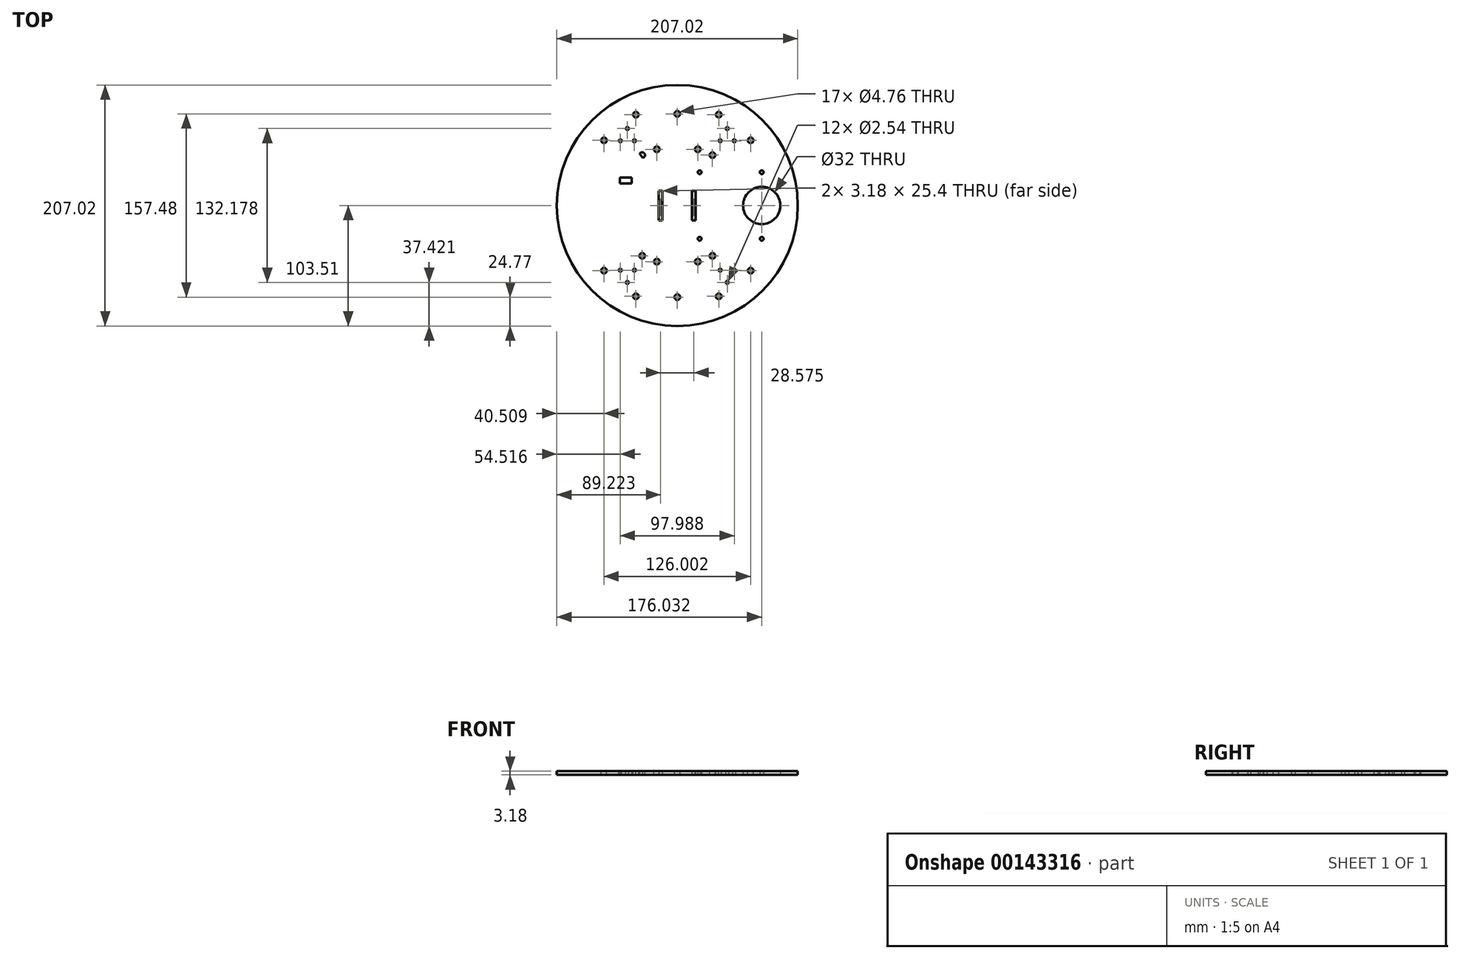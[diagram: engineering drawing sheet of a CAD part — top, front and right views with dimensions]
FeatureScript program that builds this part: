
annotation { "Feature Type Name" : "Feature", "Feature Type Description" : "" }
export const myFeature = defineFeature(function(context is Context, id is Id, definition is map)
    precondition{}
    {
        {
            var Q0;
            Q0=qCreatedBy(makeId("Top.planeOp"),FACE);
            var sketch = newSketch(context, id + "F0", { "sketchPlane" : qUnion([Q0])});
            skCircle(sketch, "E0", {"center": v(0, 0) * mm, "radius": 103.5 * mm});
            skLineSegment(sketch, "E1", {"start": v(-11.25, 102.9) * mm, "end": v(-11.25, 89.9) * mm});
            skLineSegment(sketch, "E2", {"start": v(-11.25, 89.9) * mm, "end": v(11.25, 89.9) * mm});
            skLineSegment(sketch, "E3", {"start": v(11.25, 89.9) * mm, "end": v(11.25, 102.9) * mm});
            skLineSegment(sketch, "E4", {"start": v(0, 89.9) * mm, "end": v(0, 0) * mm});
            skLineSegment(sketch, "E5.1.0", {"start": v(-83.48, -61.19) * mm, "end": v(-72.22, -54.69) * mm});
            skLineSegment(sketch, "E5.1.1", {"start": v(-72.22, -54.69) * mm, "end": v(-83.47, -35.2) * mm});
            skLineSegment(sketch, "E5.1.2", {"start": v(-83.47, -35.2) * mm, "end": v(-94.73, -41.7) * mm});
            skLineSegment(sketch, "E5.2.0", {"start": v(94.73, -41.7) * mm, "end": v(83.47, -35.2) * mm});
            skLineSegment(sketch, "E5.2.1", {"start": v(83.47, -35.2) * mm, "end": v(72.22, -54.69) * mm});
            skLineSegment(sketch, "E5.2.2", {"start": v(72.22, -54.69) * mm, "end": v(83.48, -61.19) * mm});
            skLineSegment(sketch, "E6", {"start": v(0, 0) * mm, "end": v(77.85, -44.95) * mm});
            skLineSegment(sketch, "E7", {"start": v(77.85, -44.95) * mm, "end": v(0, 0) * mm});
            skLineSegment(sketch, "E8", {"start": v(0, 0) * mm, "end": v(-77.85, -44.95) * mm});
            skSolve(sketch);
        }
        {
            var Q0;
            {var subQ2=sQuery(id+"F0.wireOp",EDGE,"E1");Q0=makeQuery(id+"F0.imprint","IMPRINT",FACE,{"disambiguationData":[TD([[makeQuery(id+"F0.imprint","IMPRINT",EDGE,{"derivedFrom":subQ2}),-1.0]])]});}
            var Q1;
            {var subQ0=sQuery(id+"F0.wireOp",EDGE,"E3");Q1=makeQuery(id+"F0.imprint","IMPRINT",FACE,{"disambiguationData":[TD([[makeQuery(id+"F0.imprint","IMPRINT",EDGE,{"derivedFrom":subQ0}),-1.0]])]});}
            var Q2;
            {var subQ4=sQuery(id+"F0.wireOp",EDGE,"E5.1.0");Q2=makeQuery(id+"F0.imprint","IMPRINT",FACE,{"disambiguationData":[TD([[makeQuery(id+"F0.imprint","IMPRINT",EDGE,{"derivedFrom":subQ4}),-1.0]])]});}
            var Q3;
            {var subQ3=sQuery(id+"F0.wireOp",EDGE,"E5.1.0");Q3=makeQuery(id+"F0.imprint","IMPRINT",FACE,{"disambiguationData":[TD([[makeQuery(id+"F0.imprint","IMPRINT",EDGE,{"derivedFrom":subQ3}),1.0]])]});}
            var Q4;
            {var subQ3=sQuery(id+"F0.wireOp",EDGE,"E5.2.0");Q4=makeQuery(id+"F0.imprint","IMPRINT",FACE,{"disambiguationData":[TD([[makeQuery(id+"F0.imprint","IMPRINT",EDGE,{"derivedFrom":subQ3}),1.0]])]});}
            var Q5;
            {var subQ3=sQuery(id+"F0.wireOp",EDGE,"E1");Q5=makeQuery(id+"F0.imprint","IMPRINT",FACE,{"disambiguationData":[TD([[makeQuery(id+"F0.imprint","IMPRINT",EDGE,{"derivedFrom":subQ3}),1.0]])]});}
            extrude(context, id + "F1", {"entities" : qUnion([Q0, Q1, Q2, Q3, Q4, Q5]), "depth" : 3.17 * mm, "offsetDistance" : 25.4 * mm});
        }
        {
            var Q0;
            Q0=makeQuery(id+"F1.opExtrude","CAP_FACE",FACE,{"disambiguationData":[OSD([sQuery(id+"F0.wireOp",EDGE,"E0"),sQuery(id+"F0.wireOp",EDGE,"E1"),sQuery(id+"F0.wireOp",EDGE,"E2"),sQuery(id+"F0.wireOp",EDGE,"E3"),sQuery(id+"F0.wireOp",EDGE,"E5.1.0"),sQuery(id+"F0.wireOp",EDGE,"E5.1.1"),sQuery(id+"F0.wireOp",EDGE,"E5.1.2"),sQuery(id+"F0.wireOp",EDGE,"E5.2.0"),sQuery(id+"F0.wireOp",EDGE,"E5.2.1"),sQuery(id+"F0.wireOp",EDGE,"E5.2.2")])],"isStart":false});
            var sketch = newSketch(context, id + "F2", { "sketchPlane" : qUnion([Q0])});
            skLineSegment(sketch, "E9", {"start": v(0, 0) * mm, "end": v(0, 58.42) * mm});
            skLineSegment(sketch, "E10", {"start": v(0, 58.42) * mm, "end": v(0, -58.42) * mm});
            skPoint(sketch, "E11", {"position": v(0, 0) * mm});
            skCircle(sketch, "E12", {"center": v(0, 58.42) * mm, "radius": 20.32 * mm});
            skCircle(sketch, "E13", {"center": v(0, -58.42) * mm, "radius": 20.32 * mm});
            skCircle(sketch, "E14", {"center": v(0, 78.74) * mm, "radius": 2.38 * mm});
            skLineSegment(sketch, "E15", {"start": v(0, 58.42) * mm, "end": v(0, 78.74) * mm});
            skLineSegment(sketch, "E16", {"start": v(0, -58.42) * mm, "end": v(0, -78.74) * mm});
            skCircle(sketch, "E17", {"center": v(0, -78.74) * mm, "radius": 2.38 * mm});
            skCircle(sketch, "E18.1.0", {"center": v(-17.6, 48.26) * mm, "radius": 2.38 * mm});
            skCircle(sketch, "E18.2.0", {"center": v(17.6, 48.26) * mm, "radius": 2.38 * mm});
            skCircle(sketch, "E19.1.0", {"center": v(17.6, -48.26) * mm, "radius": 2.38 * mm});
            skCircle(sketch, "E19.2.0", {"center": v(-17.6, -48.26) * mm, "radius": 2.38 * mm});
            skSolve(sketch);
        }
        {
            var Q0;
            {var subQ0=sQuery(id+"F2.wireOp",EDGE,"E12");var subQ1=makeQuery(id+"F2.imprint","INTERSECT",VERTEX,{"derivedFrom":[subQ0,sQuery(id+"F2.wireOp",EDGE,"E15")]});Q0=makeQuery(id+"F2.imprint","IMPRINT",FACE,{"disambiguationData":[TD([[makeQuery(id+"F2.imprint","IMPRINT",EDGE,{"disambiguationData":[TD([[subQ1,1.0]])],"derivedFrom":subQ0}),-1.0]])]});}
            var Q1;
            {var subQ0=sQuery(id+"F2.wireOp",EDGE,"E15");var subQ1=sQuery(id+"F2.wireOp",EDGE,"E12");var subQ2=makeQuery(id+"F2.imprint","INTERSECT",VERTEX,{"derivedFrom":[subQ1,subQ0]});Q1=makeQuery(id+"F2.imprint","IMPRINT",FACE,{"disambiguationData":[TD([[makeQuery(id+"F2.imprint","IMPRINT",EDGE,{"disambiguationData":[TD([[subQ2,1.0]])],"derivedFrom":subQ1}),1.0]])]});}
            var Q2;
            {var subQ0=sQuery(id+"F2.wireOp",EDGE,"E15");var subQ1=sQuery(id+"F2.wireOp",EDGE,"E12");var subQ2=makeQuery(id+"F2.imprint","INTERSECT",VERTEX,{"derivedFrom":[subQ1,subQ0]});Q2=makeQuery(id+"F2.imprint","IMPRINT",FACE,{"disambiguationData":[TD([[makeQuery(id+"F2.imprint","IMPRINT",EDGE,{"disambiguationData":[TD([[subQ2,-1.0]])],"derivedFrom":subQ1}),1.0]])]});}
            var Q3;
            {var subQ0=sQuery(id+"F2.wireOp",EDGE,"E18.1.0");var subQ1=sQuery(id+"F2.wireOp",EDGE,"E12");var subQ2=makeQuery(id+"F2.imprint","INTERSECT",VERTEX,{"disambiguationData":[OD(0.0)],"derivedFrom":[subQ1,subQ0]});Q3=makeQuery(id+"F2.imprint","IMPRINT",FACE,{"disambiguationData":[TD([[makeQuery(id+"F2.imprint","IMPRINT",EDGE,{"disambiguationData":[TD([[subQ2,-1.0]])],"derivedFrom":subQ1}),-1.0]])]});}
            var Q4;
            {var subQ0=sQuery(id+"F2.wireOp",EDGE,"E18.1.0");var subQ1=sQuery(id+"F2.wireOp",EDGE,"E12");var subQ2=makeQuery(id+"F2.imprint","INTERSECT",VERTEX,{"disambiguationData":[OD(0.0)],"derivedFrom":[subQ1,subQ0]});Q4=makeQuery(id+"F2.imprint","IMPRINT",FACE,{"disambiguationData":[TD([[makeQuery(id+"F2.imprint","IMPRINT",EDGE,{"disambiguationData":[TD([[subQ2,-1.0]])],"derivedFrom":subQ1}),1.0]])]});}
            var Q5;
            {var subQ0=sQuery(id+"F2.wireOp",EDGE,"E18.2.0");var subQ1=sQuery(id+"F2.wireOp",EDGE,"E12");var subQ2=makeQuery(id+"F2.imprint","INTERSECT",VERTEX,{"disambiguationData":[OD(0.0)],"derivedFrom":[subQ1,subQ0]});Q5=makeQuery(id+"F2.imprint","IMPRINT",FACE,{"disambiguationData":[TD([[makeQuery(id+"F2.imprint","IMPRINT",EDGE,{"disambiguationData":[TD([[subQ2,-1.0]])],"derivedFrom":subQ1}),1.0]])]});}
            var Q6;
            {var subQ0=sQuery(id+"F2.wireOp",EDGE,"E18.2.0");var subQ1=sQuery(id+"F2.wireOp",EDGE,"E12");var subQ2=makeQuery(id+"F2.imprint","INTERSECT",VERTEX,{"disambiguationData":[OD(0.0)],"derivedFrom":[subQ1,subQ0]});Q6=makeQuery(id+"F2.imprint","IMPRINT",FACE,{"disambiguationData":[TD([[makeQuery(id+"F2.imprint","IMPRINT",EDGE,{"disambiguationData":[TD([[subQ2,-1.0]])],"derivedFrom":subQ1}),-1.0]])]});}
            var Q7;
            {var subQ0=sQuery(id+"F2.wireOp",EDGE,"E19.2.0");var subQ1=sQuery(id+"F2.wireOp",EDGE,"E13");var subQ2=makeQuery(id+"F2.imprint","INTERSECT",VERTEX,{"disambiguationData":[OD(0.0)],"derivedFrom":[subQ1,subQ0]});Q7=makeQuery(id+"F2.imprint","IMPRINT",FACE,{"disambiguationData":[TD([[makeQuery(id+"F2.imprint","IMPRINT",EDGE,{"disambiguationData":[TD([[subQ2,-1.0]])],"derivedFrom":subQ1}),-1.0]])]});}
            var Q8;
            {var subQ0=sQuery(id+"F2.wireOp",EDGE,"E19.2.0");var subQ1=sQuery(id+"F2.wireOp",EDGE,"E13");var subQ2=makeQuery(id+"F2.imprint","INTERSECT",VERTEX,{"disambiguationData":[OD(0.0)],"derivedFrom":[subQ1,subQ0]});Q8=makeQuery(id+"F2.imprint","IMPRINT",FACE,{"disambiguationData":[TD([[makeQuery(id+"F2.imprint","IMPRINT",EDGE,{"disambiguationData":[TD([[subQ2,-1.0]])],"derivedFrom":subQ1}),1.0]])]});}
            var Q9;
            {var subQ0=sQuery(id+"F2.wireOp",EDGE,"E19.1.0");var subQ1=sQuery(id+"F2.wireOp",EDGE,"E13");var subQ2=makeQuery(id+"F2.imprint","INTERSECT",VERTEX,{"disambiguationData":[OD(0.0)],"derivedFrom":[subQ1,subQ0]});Q9=makeQuery(id+"F2.imprint","IMPRINT",FACE,{"disambiguationData":[TD([[makeQuery(id+"F2.imprint","IMPRINT",EDGE,{"disambiguationData":[TD([[subQ2,1.0]])],"derivedFrom":subQ1}),1.0]])]});}
            var Q10;
            {var subQ0=sQuery(id+"F2.wireOp",EDGE,"E19.1.0");var subQ1=sQuery(id+"F2.wireOp",EDGE,"E13");var subQ2=makeQuery(id+"F2.imprint","INTERSECT",VERTEX,{"disambiguationData":[OD(0.0)],"derivedFrom":[subQ1,subQ0]});Q10=makeQuery(id+"F2.imprint","IMPRINT",FACE,{"disambiguationData":[TD([[makeQuery(id+"F2.imprint","IMPRINT",EDGE,{"disambiguationData":[TD([[subQ2,1.0]])],"derivedFrom":subQ1}),-1.0]])]});}
            var Q11;
            {var subQ0=sQuery(id+"F2.wireOp",EDGE,"E16");var subQ1=sQuery(id+"F2.wireOp",EDGE,"E13");var subQ2=makeQuery(id+"F2.imprint","INTERSECT",VERTEX,{"derivedFrom":[subQ1,subQ0]});Q11=makeQuery(id+"F2.imprint","IMPRINT",FACE,{"disambiguationData":[TD([[makeQuery(id+"F2.imprint","IMPRINT",EDGE,{"disambiguationData":[TD([[subQ2,-1.0]])],"derivedFrom":subQ1}),1.0]])]});}
            var Q12;
            {var subQ0=sQuery(id+"F2.wireOp",EDGE,"E16");var subQ1=sQuery(id+"F2.wireOp",EDGE,"E13");var subQ2=makeQuery(id+"F2.imprint","INTERSECT",VERTEX,{"derivedFrom":[subQ1,subQ0]});Q12=makeQuery(id+"F2.imprint","IMPRINT",FACE,{"disambiguationData":[TD([[makeQuery(id+"F2.imprint","IMPRINT",EDGE,{"disambiguationData":[TD([[subQ2,1.0]])],"derivedFrom":subQ1}),1.0]])]});}
            var Q13;
            {var subQ0=sQuery(id+"F2.wireOp",EDGE,"E13");var subQ1=makeQuery(id+"F2.imprint","INTERSECT",VERTEX,{"derivedFrom":[subQ0,sQuery(id+"F2.wireOp",EDGE,"E16")]});Q13=makeQuery(id+"F2.imprint","IMPRINT",FACE,{"disambiguationData":[TD([[makeQuery(id+"F2.imprint","IMPRINT",EDGE,{"disambiguationData":[TD([[subQ1,1.0]])],"derivedFrom":subQ0}),-1.0]])]});}
            extrude(context, id + "F3", {"entities" : qUnion([Q0, Q1, Q2, Q3, Q4, Q5, Q6, Q7, Q8, Q9, Q10, Q11, Q12, Q13]), "operationType" : NewBodyOperationType.REMOVE, "endBound" : BoundingType.THROUGH_ALL, "oppositeDirection" : true, "depth" : 25.4 * mm, "offsetDistance" : 25.4 * mm});
        }
        {
            var Q0;
            Q0=makeQuery(id+"F1.opExtrude","CAP_FACE",FACE,{"disambiguationData":[OSD([sQuery(id+"F0.wireOp",EDGE,"E0"),sQuery(id+"F0.wireOp",EDGE,"E1"),sQuery(id+"F0.wireOp",EDGE,"E2"),sQuery(id+"F0.wireOp",EDGE,"E3"),sQuery(id+"F0.wireOp",EDGE,"E5.1.0"),sQuery(id+"F0.wireOp",EDGE,"E5.1.1"),sQuery(id+"F0.wireOp",EDGE,"E5.1.2"),sQuery(id+"F0.wireOp",EDGE,"E5.2.0"),sQuery(id+"F0.wireOp",EDGE,"E5.2.1"),sQuery(id+"F0.wireOp",EDGE,"E5.2.2")])],"isStart":false});
            var sketch = newSketch(context, id + "F4", { "sketchPlane" : qUnion([Q0])});
            skLineSegment(sketch, "E20", {"start": v(0, 0) * mm, "end": v(-42.92, 59.08) * mm});
            skLineSegment(sketch, "E21", {"start": v(-42.92, 59.08) * mm, "end": v(0, 0) * mm});
            skCircle(sketch, "E22", {"center": v(-42.92, 59.08) * mm, "radius": 20.32 * mm, "construction": true});
            skLineSegment(sketch, "E23", {"start": v(0, 117.3) * mm, "end": v(0, -119.38) * mm});
            skPoint(sketch, "E23.startSnap0", {"position": v(0, 89.9) * mm});
            skLineSegment(sketch, "E24", {"start": v(0, -119.38) * mm, "end": v(0, 117.3) * mm});
            skCircle(sketch, "E25", {"center": v(-30.18, 43.25) * mm, "radius": 2.38 * mm});
            skPoint(sketch, "E26", {"position": v(-17.6, 48.26) * mm});
            skLineSegment(sketch, "E27", {"start": v(-30.18, 43.25) * mm, "end": v(-17.6, 48.26) * mm});
            skCircle(sketch, "E28.1.0", {"center": v(-35.6, 78.03) * mm, "radius": 2.38 * mm});
            skCircle(sketch, "E28.2.0", {"center": v(-63, 55.95) * mm, "radius": 2.38 * mm});
            skLineSegment(sketch, "E29", {"start": v(0, 0) * mm, "end": v(42.92, 59.08) * mm});
            skCircle(sketch, "E30", {"center": v(42.92, 59.08) * mm, "radius": 20.32 * mm, "construction": true});
            skPoint(sketch, "E31", {"position": v(17.6, 48.26) * mm});
            skLineSegment(sketch, "E32", {"start": v(17.6, 48.26) * mm, "end": v(30.18, 43.25) * mm});
            skCircle(sketch, "E33", {"center": v(30.18, 43.25) * mm, "radius": 2.38 * mm});
            skCircle(sketch, "E34.1.0", {"center": v(63, 55.95) * mm, "radius": 2.38 * mm});
            skCircle(sketch, "E34.2.0", {"center": v(35.6, 78.03) * mm, "radius": 2.38 * mm});
            skLineSegment(sketch, "E35", {"start": v(0, 0) * mm, "end": v(-42.92, -59.08) * mm});
            skCircle(sketch, "E36", {"center": v(-42.92, -59.08) * mm, "radius": 20.32 * mm, "construction": true});
            skCircle(sketch, "E37", {"center": v(-30.18, -43.25) * mm, "radius": 2.38 * mm});
            skPoint(sketch, "E38", {"position": v(-17.6, -48.26) * mm});
            skLineSegment(sketch, "E39", {"start": v(-17.6, -48.26) * mm, "end": v(-30.18, -43.25) * mm});
            skCircle(sketch, "E40.1.0", {"center": v(-63, -55.95) * mm, "radius": 2.38 * mm});
            skCircle(sketch, "E40.2.0", {"center": v(-35.6, -78.03) * mm, "radius": 2.38 * mm});
            skLineSegment(sketch, "E41", {"start": v(0, 0) * mm, "end": v(42.92, -59.08) * mm});
            skPoint(sketch, "E42", {"position": v(17.6, -48.26) * mm});
            skCircle(sketch, "E43", {"center": v(42.92, -59.08) * mm, "radius": 20.32 * mm, "construction": true});
            skCircle(sketch, "E44", {"center": v(30.18, -43.25) * mm, "radius": 2.38 * mm});
            skLineSegment(sketch, "E45", {"start": v(17.6, -48.26) * mm, "end": v(30.18, -43.25) * mm});
            skCircle(sketch, "E46.1.0", {"center": v(35.6, -78.03) * mm, "radius": 2.38 * mm});
            skCircle(sketch, "E46.2.0", {"center": v(63, -55.95) * mm, "radius": 2.38 * mm});
            skCircle(sketch, "E47", {"center": v(-42.92, -59.08) * mm, "radius": 7.01 * mm, "construction": true});
            skCircle(sketch, "E48", {"center": v(42.92, -59.08) * mm, "radius": 7.01 * mm, "construction": true});
            skCircle(sketch, "E49", {"center": v(-42.92, 59.08) * mm, "radius": 7.01 * mm, "construction": true});
            skCircle(sketch, "E50", {"center": v(42.92, 59.08) * mm, "radius": 7.01 * mm, "construction": true});
            skCircle(sketch, "E51", {"center": v(-42.92, -66.09) * mm, "radius": 1.27 * mm});
            skCircle(sketch, "E52.1.0", {"center": v(-36.85, -55.57) * mm, "radius": 1.27 * mm});
            skCircle(sketch, "E52.2.0", {"center": v(-49, -55.57) * mm, "radius": 1.27 * mm});
            skCircle(sketch, "E53", {"center": v(42.92, -66.09) * mm, "radius": 1.27 * mm});
            skCircle(sketch, "E54.1.0", {"center": v(49, -55.57) * mm, "radius": 1.27 * mm});
            skCircle(sketch, "E54.2.0", {"center": v(36.85, -55.57) * mm, "radius": 1.27 * mm});
            skCircle(sketch, "E55", {"center": v(-42.92, 66.09) * mm, "radius": 1.27 * mm});
            skCircle(sketch, "E56.1.0", {"center": v(-49, 55.57) * mm, "radius": 1.27 * mm});
            skCircle(sketch, "E56.2.0", {"center": v(-36.85, 55.57) * mm, "radius": 1.27 * mm});
            skCircle(sketch, "E57", {"center": v(42.92, 66.09) * mm, "radius": 1.27 * mm});
            skCircle(sketch, "E58.1.0", {"center": v(36.85, 55.57) * mm, "radius": 1.27 * mm});
            skCircle(sketch, "E58.2.0", {"center": v(49, 55.57) * mm, "radius": 1.27 * mm});
            skSolve(sketch);
        }
        {
            var Q0;
            Q0=makeQuery(id+"F4.imprint","IMPRINT",FACE,{"disambiguationData":[TD([[makeQuery(id+"F4.imprint","IMPRINT",EDGE,{"derivedFrom":sQuery(id+"F4.wireOp",EDGE,"E46.2.0")}),1.0]])]});
            var Q1;
            {var subQ0=sQuery(id+"F4.wireOp",EDGE,"E44");var subQ1=sQuery(id+"F4.wireOp",EDGE,"E41");var subQ2=makeQuery(id+"F4.imprint","INTERSECT",VERTEX,{"disambiguationData":[OD(0.0)],"derivedFrom":[subQ1,subQ0]});Q1=makeQuery(id+"F4.imprint","IMPRINT",FACE,{"disambiguationData":[TD([[makeQuery(id+"F4.imprint","IMPRINT",EDGE,{"disambiguationData":[TD([[subQ2,-1.0]])],"derivedFrom":subQ1}),1.0]])]});}
            var Q2;
            {var subQ0=sQuery(id+"F4.wireOp",EDGE,"E44");var subQ4=makeQuery(id+"F4.imprint","IMPRINT",VERTEX,{"derivedFrom":subQ0});Q2=makeQuery(id+"F4.imprint","IMPRINT",FACE,{"disambiguationData":[TD([[makeQuery(id+"F4.imprint","IMPRINT",EDGE,{"disambiguationData":[TD([[subQ4,1.0]])],"derivedFrom":subQ0}),1.0]])]});}
            var Q3;
            Q3=makeQuery(id+"F4.imprint","IMPRINT",FACE,{"disambiguationData":[TD([[makeQuery(id+"F4.imprint","IMPRINT",EDGE,{"derivedFrom":sQuery(id+"F4.wireOp",EDGE,"E54.2.0")}),1.0]])]});
            var Q4;
            Q4=makeQuery(id+"F4.imprint","IMPRINT",FACE,{"disambiguationData":[TD([[makeQuery(id+"F4.imprint","IMPRINT",EDGE,{"derivedFrom":sQuery(id+"F4.wireOp",EDGE,"E54.1.0")}),1.0]])]});
            var Q5;
            Q5=makeQuery(id+"F4.imprint","IMPRINT",FACE,{"disambiguationData":[TD([[makeQuery(id+"F4.imprint","IMPRINT",EDGE,{"derivedFrom":sQuery(id+"F4.wireOp",EDGE,"E53")}),1.0]])]});
            var Q6;
            Q6=makeQuery(id+"F4.imprint","IMPRINT",FACE,{"disambiguationData":[TD([[makeQuery(id+"F4.imprint","IMPRINT",EDGE,{"derivedFrom":sQuery(id+"F4.wireOp",EDGE,"E46.1.0")}),1.0]])]});
            var Q7;
            Q7=makeQuery(id+"F4.imprint","IMPRINT",FACE,{"disambiguationData":[TD([[makeQuery(id+"F4.imprint","IMPRINT",EDGE,{"derivedFrom":sQuery(id+"F4.wireOp",EDGE,"E34.1.0")}),1.0]])]});
            var Q8;
            Q8=makeQuery(id+"F4.imprint","IMPRINT",FACE,{"disambiguationData":[TD([[makeQuery(id+"F4.imprint","IMPRINT",EDGE,{"derivedFrom":sQuery(id+"F4.wireOp",EDGE,"E58.2.0")}),1.0]])]});
            var Q9;
            Q9=makeQuery(id+"F4.imprint","IMPRINT",FACE,{"disambiguationData":[TD([[makeQuery(id+"F4.imprint","IMPRINT",EDGE,{"derivedFrom":sQuery(id+"F4.wireOp",EDGE,"E58.1.0")}),1.0]])]});
            var Q10;
            Q10=makeQuery(id+"F4.imprint","IMPRINT",FACE,{"disambiguationData":[TD([[makeQuery(id+"F4.imprint","IMPRINT",EDGE,{"derivedFrom":sQuery(id+"F4.wireOp",EDGE,"E57")}),1.0]])]});
            var Q11;
            Q11=makeQuery(id+"F4.imprint","IMPRINT",FACE,{"disambiguationData":[TD([[makeQuery(id+"F4.imprint","IMPRINT",EDGE,{"derivedFrom":sQuery(id+"F4.wireOp",EDGE,"E34.2.0")}),1.0]])]});
            var Q12;
            {var subQ0=sQuery(id+"F4.wireOp",EDGE,"E33");var subQ4=makeQuery(id+"F4.imprint","IMPRINT",VERTEX,{"derivedFrom":subQ0});Q12=makeQuery(id+"F4.imprint","IMPRINT",FACE,{"disambiguationData":[TD([[makeQuery(id+"F4.imprint","IMPRINT",EDGE,{"disambiguationData":[TD([[subQ4,1.0]])],"derivedFrom":subQ0}),1.0]])]});}
            var Q13;
            {var subQ0=sQuery(id+"F4.wireOp",EDGE,"E33");var subQ1=sQuery(id+"F4.wireOp",EDGE,"E29");var subQ2=makeQuery(id+"F4.imprint","INTERSECT",VERTEX,{"disambiguationData":[OD(0.0)],"derivedFrom":[subQ1,subQ0]});Q13=makeQuery(id+"F4.imprint","IMPRINT",FACE,{"disambiguationData":[TD([[makeQuery(id+"F4.imprint","IMPRINT",EDGE,{"disambiguationData":[TD([[subQ2,1.0]])],"derivedFrom":subQ1}),-1.0]])]});}
            var Q14;
            Q14=makeQuery(id+"F4.imprint","IMPRINT",FACE,{"disambiguationData":[TD([[makeQuery(id+"F4.imprint","IMPRINT",EDGE,{"derivedFrom":sQuery(id+"F4.wireOp",EDGE,"E28.1.0")}),1.0]])]});
            var Q15;
            Q15=makeQuery(id+"F4.imprint","IMPRINT",FACE,{"disambiguationData":[TD([[makeQuery(id+"F4.imprint","IMPRINT",EDGE,{"derivedFrom":sQuery(id+"F4.wireOp",EDGE,"E55")}),1.0]])]});
            var Q16;
            Q16=makeQuery(id+"F4.imprint","IMPRINT",FACE,{"disambiguationData":[TD([[makeQuery(id+"F4.imprint","IMPRINT",EDGE,{"derivedFrom":sQuery(id+"F4.wireOp",EDGE,"E56.2.0")}),1.0]])]});
            var Q17;
            Q17=makeQuery(id+"F4.imprint","IMPRINT",FACE,{"disambiguationData":[TD([[makeQuery(id+"F4.imprint","IMPRINT",EDGE,{"derivedFrom":sQuery(id+"F4.wireOp",EDGE,"E56.1.0")}),1.0]])]});
            var Q18;
            Q18=makeQuery(id+"F4.imprint","IMPRINT",FACE,{"disambiguationData":[TD([[makeQuery(id+"F4.imprint","IMPRINT",EDGE,{"derivedFrom":sQuery(id+"F4.wireOp",EDGE,"E28.2.0")}),1.0]])]});
            var Q19;
            {var subQ0=sQuery(id+"F4.wireOp",EDGE,"E25");var subQ4=makeQuery(id+"F4.imprint","IMPRINT",VERTEX,{"derivedFrom":subQ0});Q19=makeQuery(id+"F4.imprint","IMPRINT",FACE,{"disambiguationData":[TD([[makeQuery(id+"F4.imprint","IMPRINT",EDGE,{"disambiguationData":[TD([[subQ4,-1.0]])],"derivedFrom":subQ0}),1.0]])]});}
            var Q20;
            {var subQ0=sQuery(id+"F4.wireOp",EDGE,"E25");var subQ1=sQuery(id+"F4.wireOp",EDGE,"E21");var subQ2=makeQuery(id+"F4.imprint","INTERSECT",VERTEX,{"disambiguationData":[OD(0.0)],"derivedFrom":[subQ1,subQ0]});Q20=makeQuery(id+"F4.imprint","IMPRINT",FACE,{"disambiguationData":[TD([[makeQuery(id+"F4.imprint","IMPRINT",EDGE,{"disambiguationData":[TD([[subQ2,-1.0]])],"derivedFrom":subQ1}),-1.0]])]});}
            var Q21;
            {var subQ0=sQuery(id+"F4.wireOp",EDGE,"E37");var subQ4=makeQuery(id+"F4.imprint","IMPRINT",VERTEX,{"derivedFrom":subQ0});Q21=makeQuery(id+"F4.imprint","IMPRINT",FACE,{"disambiguationData":[TD([[makeQuery(id+"F4.imprint","IMPRINT",EDGE,{"disambiguationData":[TD([[subQ4,1.0]])],"derivedFrom":subQ0}),1.0]])]});}
            var Q22;
            {var subQ0=sQuery(id+"F4.wireOp",EDGE,"E37");var subQ1=sQuery(id+"F4.wireOp",EDGE,"E35");var subQ2=makeQuery(id+"F4.imprint","INTERSECT",VERTEX,{"disambiguationData":[OD(0.0)],"derivedFrom":[subQ1,subQ0]});Q22=makeQuery(id+"F4.imprint","IMPRINT",FACE,{"disambiguationData":[TD([[makeQuery(id+"F4.imprint","IMPRINT",EDGE,{"disambiguationData":[TD([[subQ2,1.0]])],"derivedFrom":subQ1}),-1.0]])]});}
            var Q23;
            Q23=makeQuery(id+"F4.imprint","IMPRINT",FACE,{"disambiguationData":[TD([[makeQuery(id+"F4.imprint","IMPRINT",EDGE,{"derivedFrom":sQuery(id+"F4.wireOp",EDGE,"E52.1.0")}),1.0]])]});
            var Q24;
            Q24=makeQuery(id+"F4.imprint","IMPRINT",FACE,{"disambiguationData":[TD([[makeQuery(id+"F4.imprint","IMPRINT",EDGE,{"derivedFrom":sQuery(id+"F4.wireOp",EDGE,"E51")}),1.0]])]});
            var Q25;
            Q25=makeQuery(id+"F4.imprint","IMPRINT",FACE,{"disambiguationData":[TD([[makeQuery(id+"F4.imprint","IMPRINT",EDGE,{"derivedFrom":sQuery(id+"F4.wireOp",EDGE,"E52.2.0")}),1.0]])]});
            var Q26;
            Q26=makeQuery(id+"F4.imprint","IMPRINT",FACE,{"disambiguationData":[TD([[makeQuery(id+"F4.imprint","IMPRINT",EDGE,{"derivedFrom":sQuery(id+"F4.wireOp",EDGE,"E40.1.0")}),1.0]])]});
            var Q27;
            Q27=makeQuery(id+"F4.imprint","IMPRINT",FACE,{"disambiguationData":[TD([[makeQuery(id+"F4.imprint","IMPRINT",EDGE,{"derivedFrom":sQuery(id+"F4.wireOp",EDGE,"E40.2.0")}),1.0]])]});
            extrude(context, id + "F5", {"entities" : qUnion([Q0, Q1, Q2, Q3, Q4, Q5, Q6, Q7, Q8, Q9, Q10, Q11, Q12, Q13, Q14, Q15, Q16, Q17, Q18, Q19, Q20, Q21, Q22, Q23, Q24, Q25, Q26, Q27]), "operationType" : NewBodyOperationType.REMOVE, "endBound" : BoundingType.THROUGH_ALL, "oppositeDirection" : true, "depth" : 25.4 * mm, "offsetDistance" : 25.4 * mm});
        }
        {
            var Q0;
            Q0=makeQuery(id+"F1.opExtrude","CAP_FACE",FACE,{"disambiguationData":[OSD([sQuery(id+"F0.wireOp",EDGE,"E0"),sQuery(id+"F0.wireOp",EDGE,"E1"),sQuery(id+"F0.wireOp",EDGE,"E2"),sQuery(id+"F0.wireOp",EDGE,"E3"),sQuery(id+"F0.wireOp",EDGE,"E5.1.0"),sQuery(id+"F0.wireOp",EDGE,"E5.1.1"),sQuery(id+"F0.wireOp",EDGE,"E5.1.2"),sQuery(id+"F0.wireOp",EDGE,"E5.2.0"),sQuery(id+"F0.wireOp",EDGE,"E5.2.1"),sQuery(id+"F0.wireOp",EDGE,"E5.2.2")])],"isStart":true});
            var sketch = newSketch(context, id + "F6", { "sketchPlane" : qUnion([Q0])});
            skLineSegment(sketch, "E59.bottom", {"start": v(72.52, 28.58) * mm, "end": v(19.18, 28.58) * mm});
            skLineSegment(sketch, "E59.top", {"start": v(72.52, -28.58) * mm, "end": v(19.18, -28.58) * mm});
            skLineSegment(sketch, "E59.left", {"start": v(72.52, 28.58) * mm, "end": v(72.52, -28.58) * mm});
            skLineSegment(sketch, "E59.right", {"start": v(19.18, 28.58) * mm, "end": v(19.18, -28.58) * mm});
            skPoint(sketch, "E59.middle", {"position": v(45.85, 0) * mm});
            skCircle(sketch, "E60", {"center": v(19.18, 28.58) * mm, "radius": 1.59 * mm});
            skCircle(sketch, "E61", {"center": v(72.52, 28.58) * mm, "radius": 1.59 * mm});
            skCircle(sketch, "E62", {"center": v(19.18, -28.58) * mm, "radius": 1.59 * mm});
            skCircle(sketch, "E63", {"center": v(72.52, -28.58) * mm, "radius": 1.59 * mm});
            skCircle(sketch, "E64", {"center": v(72.52, 0) * mm, "radius": 16 * mm});
            skLineSegment(sketch, "E65.bottom", {"start": v(-39.07, -18.9) * mm, "end": v(-49.23, -18.9) * mm});
            skLineSegment(sketch, "E65.top", {"start": v(-39.07, -23.98) * mm, "end": v(-49.23, -23.98) * mm});
            skLineSegment(sketch, "E65.left", {"start": v(-39.07, -18.9) * mm, "end": v(-39.07, -23.98) * mm});
            skLineSegment(sketch, "E65.right", {"start": v(-49.23, -18.9) * mm, "end": v(-49.23, -23.98) * mm});
            skPoint(sketch, "E65.middle", {"position": v(-44.15, -21.44) * mm});
            skLineSegment(sketch, "E66.bottom", {"start": v(-12.7, 50.8) * mm, "end": v(12.7, 50.8) * mm});
            skLineSegment(sketch, "E66.top", {"start": v(-12.7, -50.8) * mm, "end": v(12.7, -50.8) * mm});
            skLineSegment(sketch, "E66.left", {"start": v(-12.7, 50.8) * mm, "end": v(-12.7, -50.8) * mm});
            skLineSegment(sketch, "E66.right", {"start": v(12.7, 50.8) * mm, "end": v(12.7, -50.8) * mm});
            skPoint(sketch, "E66.middle", {"position": v(0, 0) * mm});
            skLineSegment(sketch, "E67.bottom", {"start": v(-38.35, 32) * mm, "end": v(-66.29, 32) * mm});
            skLineSegment(sketch, "E67.top", {"start": v(-38.35, -11.19) * mm, "end": v(-66.29, -11.19) * mm});
            skLineSegment(sketch, "E67.left", {"start": v(-38.35, 32) * mm, "end": v(-38.35, -11.19) * mm});
            skLineSegment(sketch, "E67.right", {"start": v(-66.29, 32) * mm, "end": v(-66.29, -11.19) * mm});
            skPoint(sketch, "E67.middle", {"position": v(-52.32, 10.4) * mm});
            skLineSegment(sketch, "E68.bottom", {"start": v(-12.7, -12.7) * mm, "end": v(-15.88, -12.7) * mm});
            skLineSegment(sketch, "E68.top", {"start": v(-12.7, 12.7) * mm, "end": v(-15.88, 12.7) * mm});
            skLineSegment(sketch, "E68.left", {"start": v(-12.7, -12.7) * mm, "end": v(-12.7, 12.7) * mm});
            skLineSegment(sketch, "E68.right", {"start": v(-15.88, -12.7) * mm, "end": v(-15.88, 12.7) * mm});
            skPoint(sketch, "E68.middle", {"position": v(-14.29, 0) * mm});
            skPoint(sketch, "E68.middle.positionSnap0", {"position": v(-12.7, 0) * mm});
            skPoint(sketch, "E68.centerSnap0", {"position": v(-12.7, 0) * mm});
            skLineSegment(sketch, "E69.bottom", {"start": v(12.7, -12.7) * mm, "end": v(15.88, -12.7) * mm});
            skLineSegment(sketch, "E69.top", {"start": v(12.7, 12.7) * mm, "end": v(15.88, 12.7) * mm});
            skLineSegment(sketch, "E69.left", {"start": v(12.7, -12.7) * mm, "end": v(12.7, 12.7) * mm});
            skLineSegment(sketch, "E69.right", {"start": v(15.88, -12.7) * mm, "end": v(15.88, 12.7) * mm});
            skPoint(sketch, "E69.middle", {"position": v(14.29, 0) * mm});
            skPoint(sketch, "E69.middle.positionSnap0", {"position": v(12.7, 0) * mm});
            skPoint(sketch, "E69.centerSnap0", {"position": v(12.7, 0) * mm});
            skSolve(sketch);
        }
        {
            var Q0;
            Q0=makeQuery(id+"F6.imprint","IMPRINT",FACE,{"disambiguationData":[TD([[makeQuery(id+"F6.imprint","IMPRINT",EDGE,{"derivedFrom":sQuery(id+"F6.wireOp",EDGE,"E65.bottom")}),1.0]])]});
            var Q1;
            Q1=makeQuery(id+"F6.imprint","IMPRINT",FACE,{"disambiguationData":[TD([[makeQuery(id+"F6.imprint","IMPRINT",EDGE,{"derivedFrom":sQuery(id+"F6.wireOp",EDGE,"E68.bottom")}),-1.0]])]});
            var Q2;
            Q2=makeQuery(id+"F6.imprint","IMPRINT",FACE,{"disambiguationData":[TD([[makeQuery(id+"F6.imprint","IMPRINT",EDGE,{"derivedFrom":sQuery(id+"F6.wireOp",EDGE,"E69.bottom")}),1.0]])]});
            var Q3;
            {var subQ0=sQuery(id+"F6.wireOp",EDGE,"E64");var subQ1=sQuery(id+"F6.wireOp",EDGE,"E59.left");var subQ2=makeQuery(id+"F6.imprint","INTERSECT",VERTEX,{"disambiguationData":[OD(0.0)],"derivedFrom":[subQ1,subQ0]});Q3=makeQuery(id+"F6.imprint","IMPRINT",FACE,{"disambiguationData":[TD([[makeQuery(id+"F6.imprint","IMPRINT",EDGE,{"disambiguationData":[TD([[subQ2,-1.0]])],"derivedFrom":subQ1}),-1.0]])]});}
            var Q4;
            {var subQ0=sQuery(id+"F6.wireOp",EDGE,"E64");var subQ1=sQuery(id+"F6.wireOp",EDGE,"E59.left");var subQ2=makeQuery(id+"F6.imprint","INTERSECT",VERTEX,{"disambiguationData":[OD(0.0)],"derivedFrom":[subQ1,subQ0]});Q4=makeQuery(id+"F6.imprint","IMPRINT",FACE,{"disambiguationData":[TD([[makeQuery(id+"F6.imprint","IMPRINT",EDGE,{"disambiguationData":[TD([[subQ2,-1.0]])],"derivedFrom":subQ1}),1.0]])]});}
            var Q5;
            {var subQ0=sQuery(id+"F6.wireOp",EDGE,"E59.right");var subQ1=sQuery(id+"F6.wireOp",EDGE,"E59.top");var subQ2=makeQuery(id+"F6.imprint","INTERSECT",VERTEX,{"derivedFrom":[subQ1,subQ0]});Q5=makeQuery(id+"F6.imprint","IMPRINT",FACE,{"disambiguationData":[TD([[makeQuery(id+"F6.imprint","IMPRINT",EDGE,{"disambiguationData":[TD([[subQ2,1.0]])],"derivedFrom":subQ1}),1.0]])]});}
            var Q6;
            {var subQ0=sQuery(id+"F6.wireOp",EDGE,"E59.right");var subQ1=sQuery(id+"F6.wireOp",EDGE,"E59.top");var subQ2=makeQuery(id+"F6.imprint","INTERSECT",VERTEX,{"derivedFrom":[subQ1,subQ0]});Q6=makeQuery(id+"F6.imprint","IMPRINT",FACE,{"disambiguationData":[TD([[makeQuery(id+"F6.imprint","IMPRINT",EDGE,{"disambiguationData":[TD([[subQ2,1.0]])],"derivedFrom":subQ1}),-1.0]])]});}
            var Q7;
            {var subQ0=sQuery(id+"F6.wireOp",EDGE,"E59.left");var subQ1=sQuery(id+"F6.wireOp",EDGE,"E59.top");var subQ2=makeQuery(id+"F6.imprint","INTERSECT",VERTEX,{"derivedFrom":[subQ1,subQ0]});Q7=makeQuery(id+"F6.imprint","IMPRINT",FACE,{"disambiguationData":[TD([[makeQuery(id+"F6.imprint","IMPRINT",EDGE,{"disambiguationData":[TD([[subQ2,-1.0]])],"derivedFrom":subQ1}),-1.0]])]});}
            var Q8;
            {var subQ0=sQuery(id+"F6.wireOp",EDGE,"E59.left");var subQ1=sQuery(id+"F6.wireOp",EDGE,"E59.top");var subQ2=makeQuery(id+"F6.imprint","INTERSECT",VERTEX,{"derivedFrom":[subQ1,subQ0]});Q8=makeQuery(id+"F6.imprint","IMPRINT",FACE,{"disambiguationData":[TD([[makeQuery(id+"F6.imprint","IMPRINT",EDGE,{"disambiguationData":[TD([[subQ2,-1.0]])],"derivedFrom":subQ1}),1.0]])]});}
            var Q9;
            {var subQ0=sQuery(id+"F6.wireOp",EDGE,"E59.right");var subQ1=sQuery(id+"F6.wireOp",EDGE,"E59.bottom");var subQ2=makeQuery(id+"F6.imprint","INTERSECT",VERTEX,{"derivedFrom":[subQ1,subQ0]});Q9=makeQuery(id+"F6.imprint","IMPRINT",FACE,{"disambiguationData":[TD([[makeQuery(id+"F6.imprint","IMPRINT",EDGE,{"disambiguationData":[TD([[subQ2,1.0]])],"derivedFrom":subQ1}),-1.0]])]});}
            var Q10;
            {var subQ0=sQuery(id+"F6.wireOp",EDGE,"E59.right");var subQ1=sQuery(id+"F6.wireOp",EDGE,"E59.bottom");var subQ2=makeQuery(id+"F6.imprint","INTERSECT",VERTEX,{"derivedFrom":[subQ1,subQ0]});Q10=makeQuery(id+"F6.imprint","IMPRINT",FACE,{"disambiguationData":[TD([[makeQuery(id+"F6.imprint","IMPRINT",EDGE,{"disambiguationData":[TD([[subQ2,1.0]])],"derivedFrom":subQ1}),1.0]])]});}
            var Q11;
            {var subQ0=sQuery(id+"F6.wireOp",EDGE,"E59.left");var subQ1=sQuery(id+"F6.wireOp",EDGE,"E59.bottom");var subQ2=makeQuery(id+"F6.imprint","INTERSECT",VERTEX,{"derivedFrom":[subQ1,subQ0]});Q11=makeQuery(id+"F6.imprint","IMPRINT",FACE,{"disambiguationData":[TD([[makeQuery(id+"F6.imprint","IMPRINT",EDGE,{"disambiguationData":[TD([[subQ2,-1.0]])],"derivedFrom":subQ1}),1.0]])]});}
            var Q12;
            {var subQ0=sQuery(id+"F6.wireOp",EDGE,"E59.left");var subQ1=sQuery(id+"F6.wireOp",EDGE,"E59.bottom");var subQ2=makeQuery(id+"F6.imprint","INTERSECT",VERTEX,{"derivedFrom":[subQ1,subQ0]});Q12=makeQuery(id+"F6.imprint","IMPRINT",FACE,{"disambiguationData":[TD([[makeQuery(id+"F6.imprint","IMPRINT",EDGE,{"disambiguationData":[TD([[subQ2,-1.0]])],"derivedFrom":subQ1}),-1.0]])]});}
            extrude(context, id + "F7", {"entities" : qUnion([Q0, Q1, Q2, Q3, Q4, Q5, Q6, Q7, Q8, Q9, Q10, Q11, Q12]), "operationType" : NewBodyOperationType.REMOVE, "endBound" : BoundingType.THROUGH_ALL, "oppositeDirection" : true, "depth" : 25.4 * mm, "offsetDistance" : 25.4 * mm});
        }
    });
